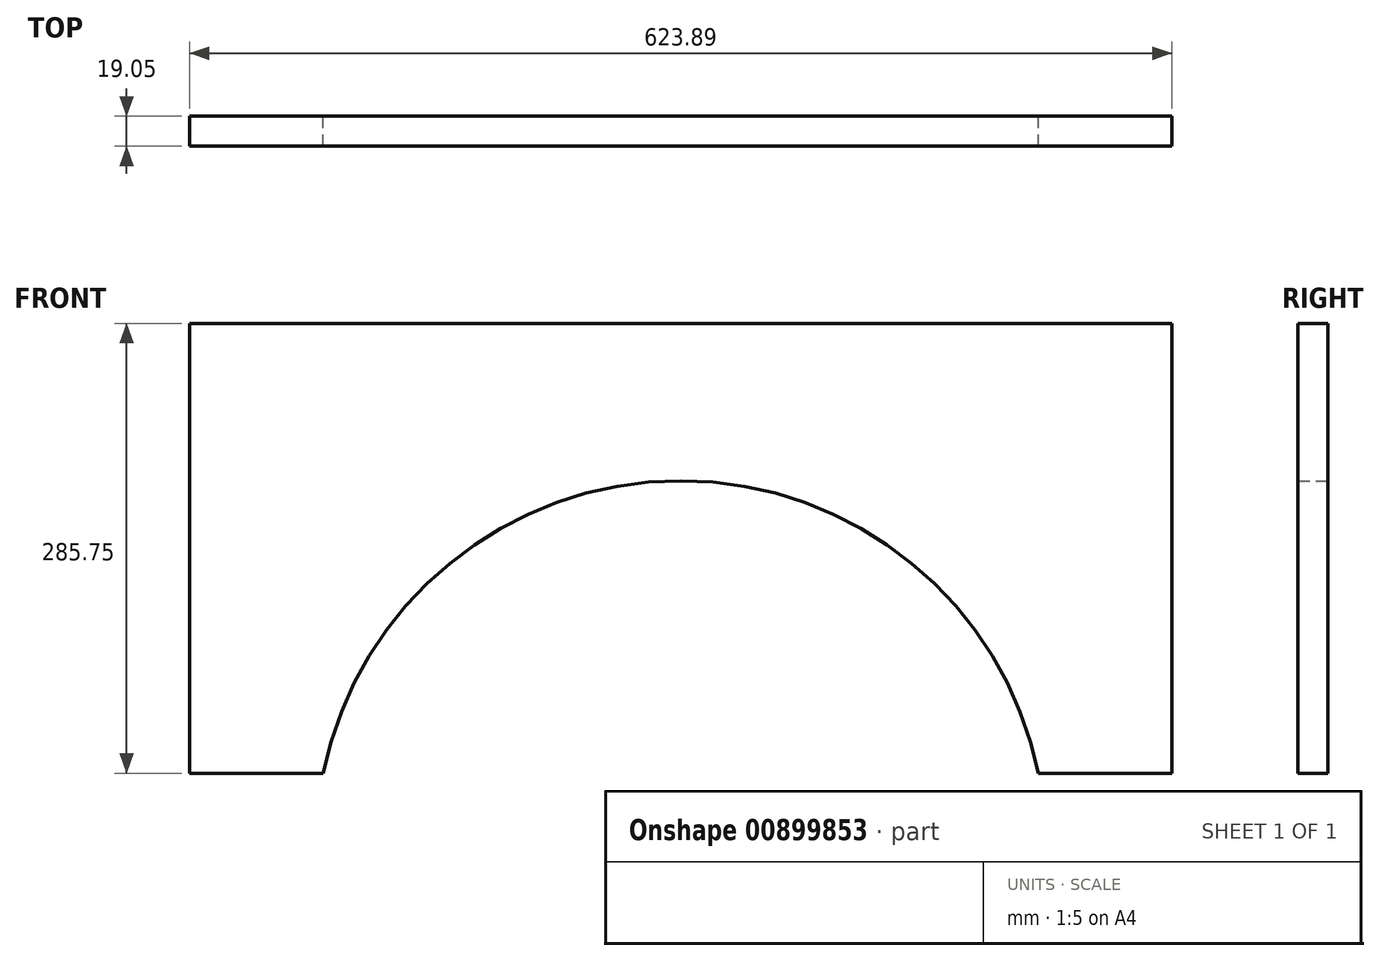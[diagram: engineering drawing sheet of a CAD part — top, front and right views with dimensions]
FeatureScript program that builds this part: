
annotation { "Feature Type Name" : "Feature", "Feature Type Description" : "" }
export const myFeature = defineFeature(function(context is Context, id is Id, definition is map)
    precondition{}
    {
        {
            var Q0;
            Q0=qCreatedBy(makeId("Front.planeOp"),FACE);
            var sketch = newSketch(context, id + "F0", { "sketchPlane" : qUnion([Q0])});
            skLineSegment(sketch, "E0", {"start": v(334.1, 149.07) * mm, "end": v(-289.79, 149.07) * mm});
            skLineSegment(sketch, "E1", {"start": v(-289.79, 149.07) * mm, "end": v(-289.79, -136.68) * mm});
            skLineSegment(sketch, "E2", {"start": v(-289.79, -136.68) * mm, "end": v(-204.88, -136.68) * mm});
            skLineSegment(sketch, "E3", {"start": v(334.1, 149.07) * mm, "end": v(334.1, -136.68) * mm});
            skLineSegment(sketch, "E4", {"start": v(334.1, -136.68) * mm, "end": v(249.2, -136.68) * mm});
            skArc(sketch, "E5", {"start": v(249.2, -136.68) * mm, "mid": v(22.16, 49.05) * mm, "end": v(-204.88, -136.68) * mm});
            skSolve(sketch);
        }
        {
            var Q0;
            Q0 = qSketchRegion(id + "F0", true);
            extrude(context, id + "F1", {"entities" : qUnion([Q0]), "depth" : 19.05 * mm, "offsetDistance" : 25.4 * mm});
        }
    });
